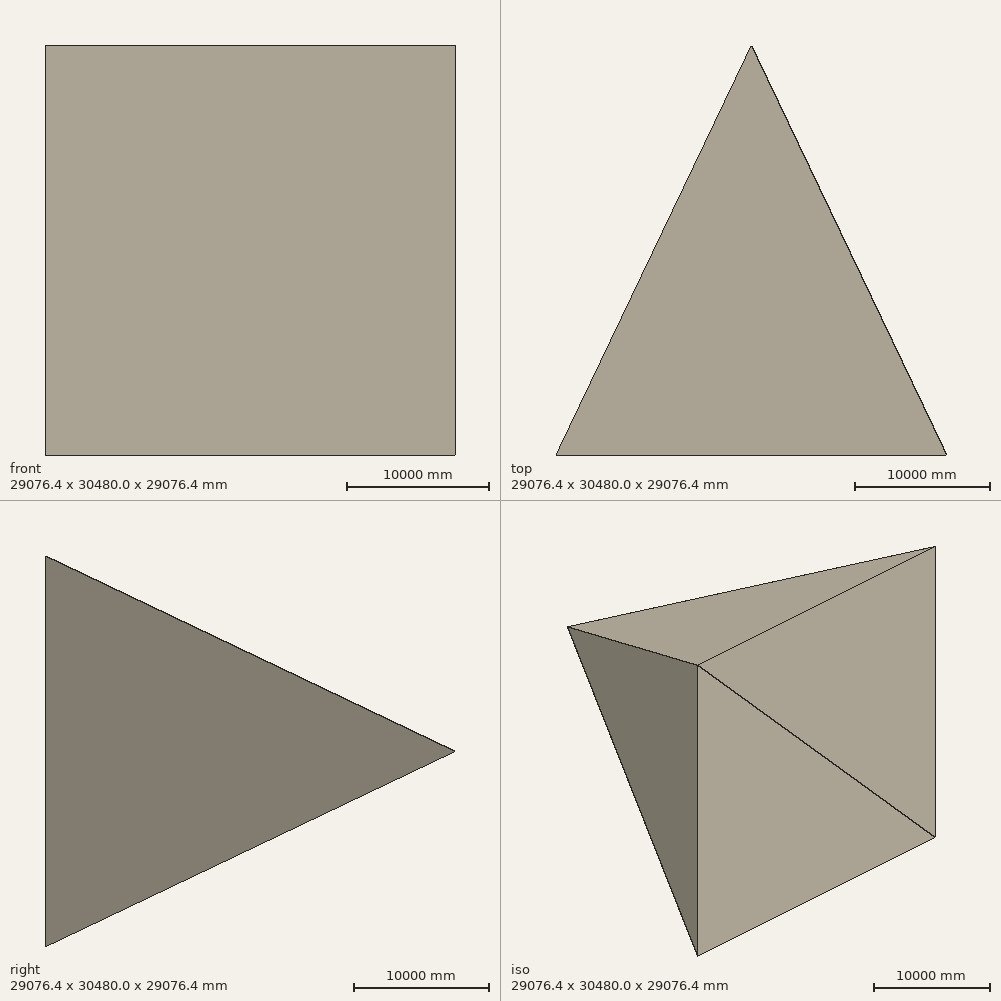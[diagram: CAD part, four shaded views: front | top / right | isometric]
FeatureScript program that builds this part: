
annotation { "Feature Type Name" : "Feature", "Feature Type Description" : "" }
export const myFeature = defineFeature(function(context is Context, id is Id, definition is map)
    precondition{}
    {
        {
            var Q0;
            Q0=qCreatedBy(makeId("Top.planeOp"),FACE);
            var sketch = newSketch(context, id + "F0", { "sketchPlane" : qUnion([Q0])});
            skLineSegment(sketch, "E0", {"start": v(0, 0) * mm, "end": v(14538.21, -30480) * mm});
            skLineSegment(sketch, "E1", {"start": v(0, 0) * mm, "end": v(-14538.21, -30480) * mm});
            skLineSegment(sketch, "E2", {"start": v(-14538.21, -30480) * mm, "end": v(14538.21, -30480) * mm});
            skSolve(sketch);
        }
        {
            var Q0;
            Q0=qCreatedBy(makeId("Right.planeOp"),FACE);
            var sketch = newSketch(context, id + "F1", { "sketchPlane" : qUnion([Q0])});
            skLineSegment(sketch, "E3", {"start": v(0, 0) * mm, "end": v(-30480, 14538.21) * mm});
            skLineSegment(sketch, "E4", {"start": v(0, 0) * mm, "end": v(-30480, -14538.21) * mm});
            skLineSegment(sketch, "E5", {"start": v(-30480, 14538.21) * mm, "end": v(-30480, -14538.21) * mm});
            skSolve(sketch);
        }
        {
            var Q0;
            Q0=makeQuery(id+"F0.imprint","IMPRINT",FACE,{"disambiguationData":[TD([[makeQuery(id+"F0.imprint","IMPRINT",EDGE,{"derivedFrom":sQuery(id+"F0.wireOp",EDGE,"E0")}),-1.0]])]});
            var Q1;
            Q1=sQuery(id+"F1.wireOp",VERTEX,"E5.start");
            var Q2;
            Q2=sQuery(id+"F1.wireOp",VERTEX,"E4.end");
            extrude(context, id + "F2", {"entities" : qUnion([Q0]), "endBound" : BoundingType.UP_TO_VERTEX, "endBoundEntityVertex" : qUnion([Q1]), "depth" : 25.4 * mm, "hasSecondDirection" : true, "secondDirectionBound" : SecondDirectionBoundingType.UP_TO_VERTEX, "secondDirectionOppositeDirection" : true, "secondDirectionBoundEntityVertex" : qUnion([Q2]), "secondDirectionDepth" : 25.4 * mm});
        }
        {
            var Q0;
            Q0 = qSketchRegion(id + "F1", true);
            var Q1;
            Q1=sQuery(id+"F0.wireOp",VERTEX,"E2.end");
            var Q2;
            Q2=sQuery(id+"F0.wireOp",VERTEX,"E2.start");
            extrude(context, id + "F3", {"entities" : qUnion([Q0]), "operationType" : NewBodyOperationType.INTERSECT, "endBound" : BoundingType.UP_TO_VERTEX, "endBoundEntityVertex" : qUnion([Q1]), "depth" : 25.4 * mm, "hasSecondDirection" : true, "secondDirectionBound" : SecondDirectionBoundingType.UP_TO_VERTEX, "secondDirectionOppositeDirection" : true, "secondDirectionBoundEntityVertex" : qUnion([Q2]), "secondDirectionDepth" : 25.4 * mm});
        }
    });
